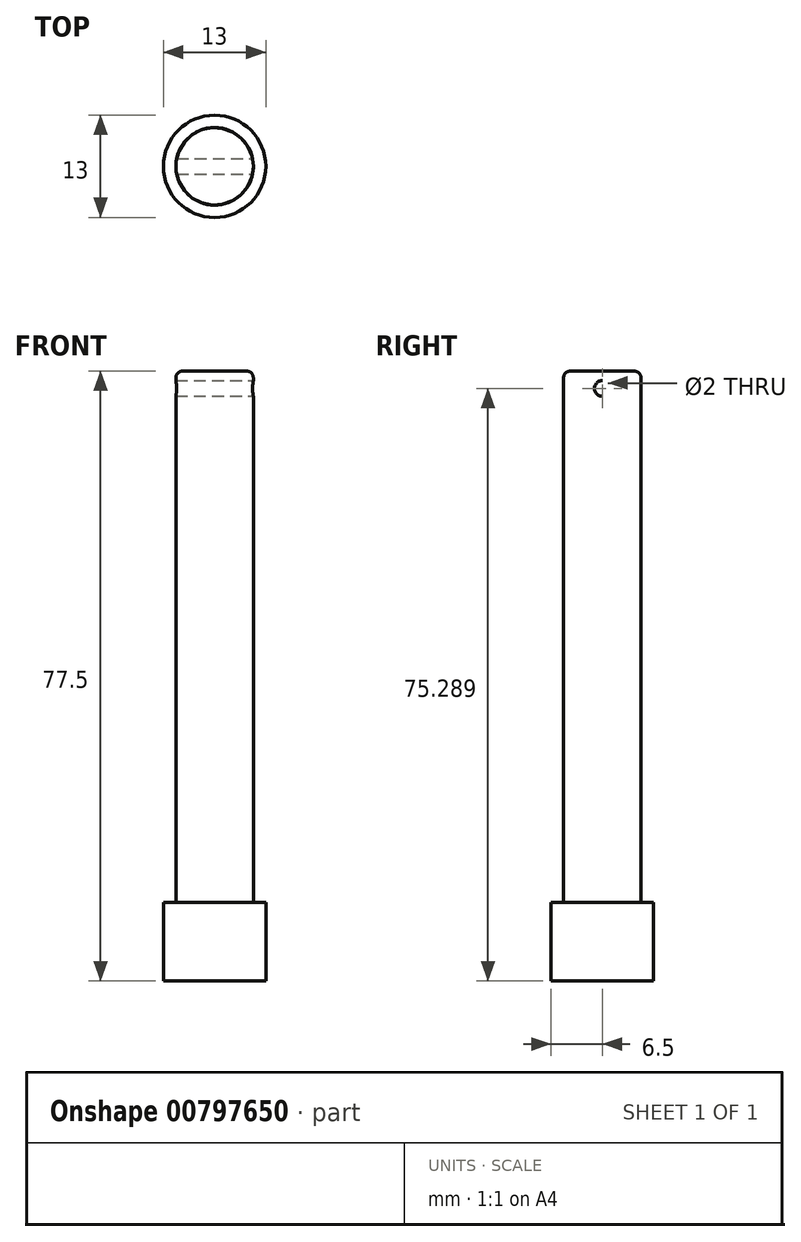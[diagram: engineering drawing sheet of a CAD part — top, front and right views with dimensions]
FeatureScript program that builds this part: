
annotation { "Feature Type Name" : "Feature", "Feature Type Description" : "" }
export const myFeature = defineFeature(function(context is Context, id is Id, definition is map)
    precondition{}
    {
        {
            var Q0;
            Q0=qCreatedBy(makeId("Top.planeOp"),FACE);
            var sketch = newSketch(context, id + "F0", { "sketchPlane" : qUnion([Q0])});
            skCircle(sketch, "E0", {"center": v(0, 0) * mm, "radius": 6.5 * mm});
            skCircle(sketch, "E1", {"center": v(0, 0) * mm, "radius": 4.92 * mm});
            skSolve(sketch);
        }
        {
            var Q0;
            Q0 = qSketchRegion(id + "F0", true);
            var Q1;
            Q1=makeQuery(id+"F0.imprint","IMPRINT",FACE,{"disambiguationData":[TD([[makeQuery(id+"F0.imprint","IMPRINT",EDGE,{"derivedFrom":sQuery(id+"F0.wireOp",EDGE,"E1")}),1.0]])]});
            extrude(context, id + "F1", {"entities" : qUnion([Q0, Q1]), "oppositeDirection" : true, "depth" : 10 * mm, "offsetDistance" : 25 * mm});
        }
        {
            var Q0;
            Q0=makeQuery(id+"F1.opExtrude","CAP_FACE",FACE,{"disambiguationData":[OSD([sQuery(id+"F0.wireOp",EDGE,"E0")])],"isStart":true});
            var sketch = newSketch(context, id + "F2", { "sketchPlane" : qUnion([Q0])});
            skCircle(sketch, "E2", {"center": v(0, 0) * mm, "radius": 4.92 * mm});
            skSolve(sketch);
        }
        {
            var Q0;
            Q0 = qSketchRegion(id + "F2", true);
            extrude(context, id + "F3", {"entities" : qUnion([Q0]), "operationType" : NewBodyOperationType.ADD, "depth" : 67.5 * mm, "offsetDistance" : 25 * mm});
        }
        {
            var Q0;
            Q0=makeQuery(id+"F3.opExtrude","CAP_EDGE",EDGE,{"disambiguationData":[OSD([sQuery(id+"F2.wireOp",EDGE,"E2")])],"isStart":false});
            fillet(context, id + "F4", {"entities" : qUnion([Q0]), "radius" : 1 * mm, "tangentPropagation" : true, "rho" : 0.5, "crossSection" : FilletCrossSection.CONIC, "allowEdgeOverflow" : false});
        }
        {
            var Q0;
            Q0=qCreatedBy(makeId("Right.planeOp"),FACE);
            var sketch = newSketch(context, id + "F5", { "sketchPlane" : qUnion([Q0])});
            skCircle(sketch, "E3", {"center": v(0, 65.29) * mm, "radius": 1 * mm});
            skSolve(sketch);
        }
        {
            var Q0;
            Q0 = qSketchRegion(id + "F5", true);
            extrude(context, id + "F6", {"entities" : qUnion([Q0]), "operationType" : NewBodyOperationType.REMOVE, "endBound" : BoundingType.SYMMETRIC, "oppositeDirection" : true, "depth" : 25 * mm, "offsetDistance" : 25 * mm});
        }
    });
